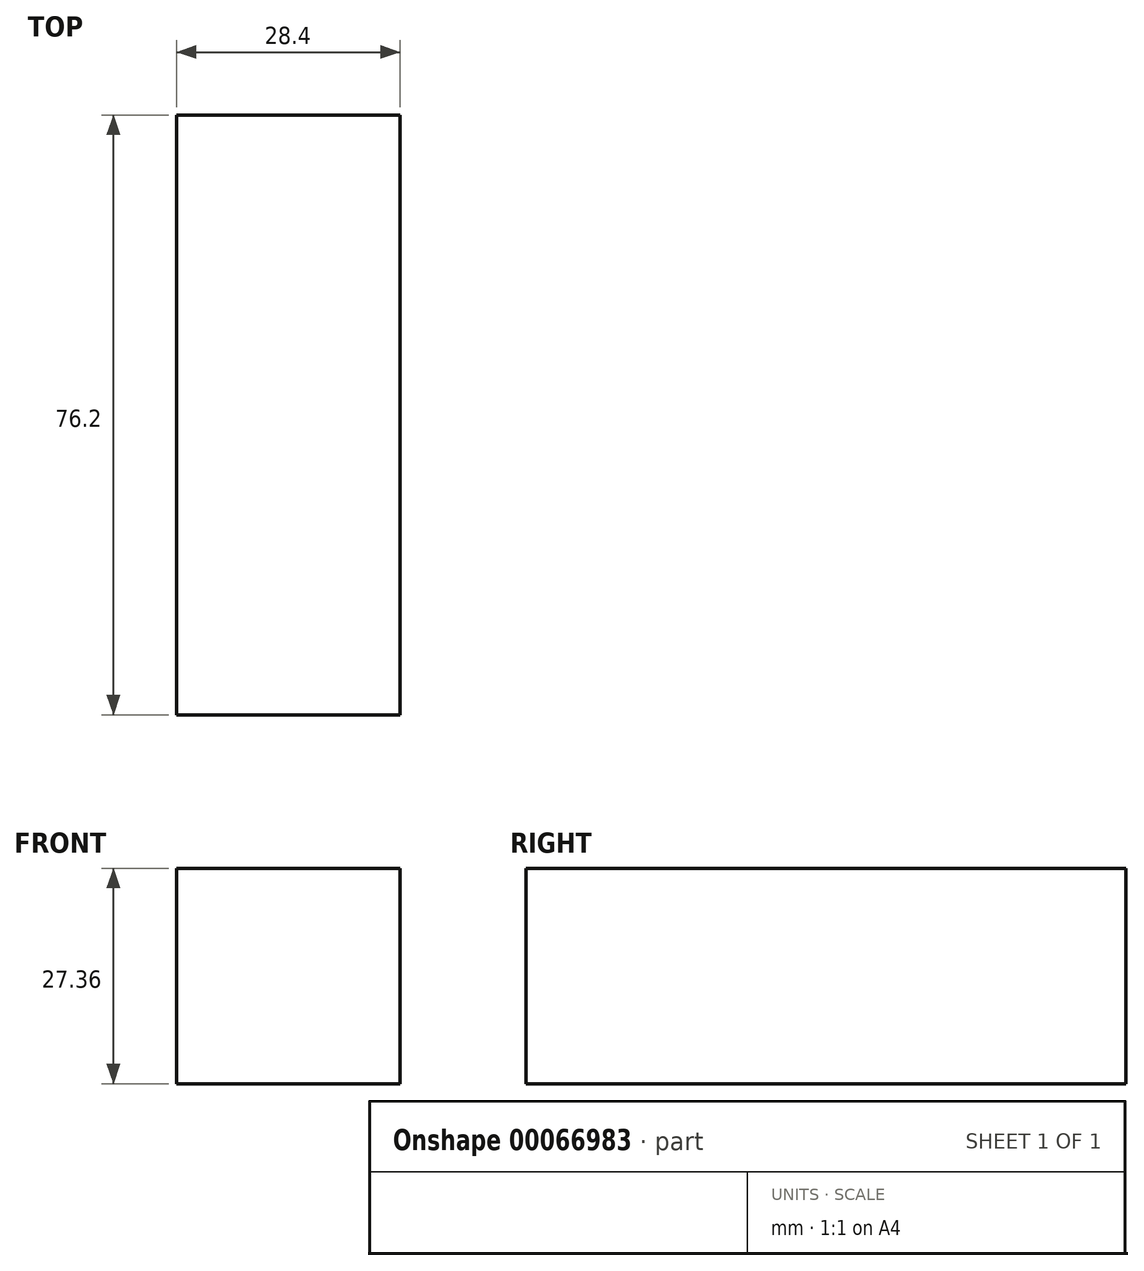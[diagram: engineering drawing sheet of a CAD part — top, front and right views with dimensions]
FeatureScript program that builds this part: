
annotation { "Feature Type Name" : "Feature", "Feature Type Description" : "" }
export const myFeature = defineFeature(function(context is Context, id is Id, definition is map)
    precondition{}
    {
        {
            var Q0;
            Q0=qCreatedBy(makeId("Front.planeOp"),FACE);
            var sketch = newSketch(context, id + "F0", { "sketchPlane" : qUnion([Q0])});
            skLineSegment(sketch, "E0", {"start": v(0, 0) * mm, "end": v(28.4, 0) * mm});
            skLineSegment(sketch, "E1", {"start": v(28.4, 0) * mm, "end": v(28.4, 27.36) * mm});
            skLineSegment(sketch, "E2", {"start": v(28.4, 27.36) * mm, "end": v(0, 27.36) * mm});
            skLineSegment(sketch, "E3", {"start": v(0, 27.36) * mm, "end": v(0, -1.73) * mm});
            skSolve(sketch);
        }
        {
            var Q0;
            {var subQ0=sQuery(id+"F0.wireOp",EDGE,"E0");Q0=makeQuery(id+"F0.imprint","IMPRINT",FACE,{"disambiguationData":[TD([[makeQuery(id+"F0.imprint","IMPRINT",EDGE,{"derivedFrom":subQ0}),1.0]])]});}
            extrude(context, id + "F1", {"entities" : qUnion([Q0]), "depth" : 76.2 * mm});
        }
    });
